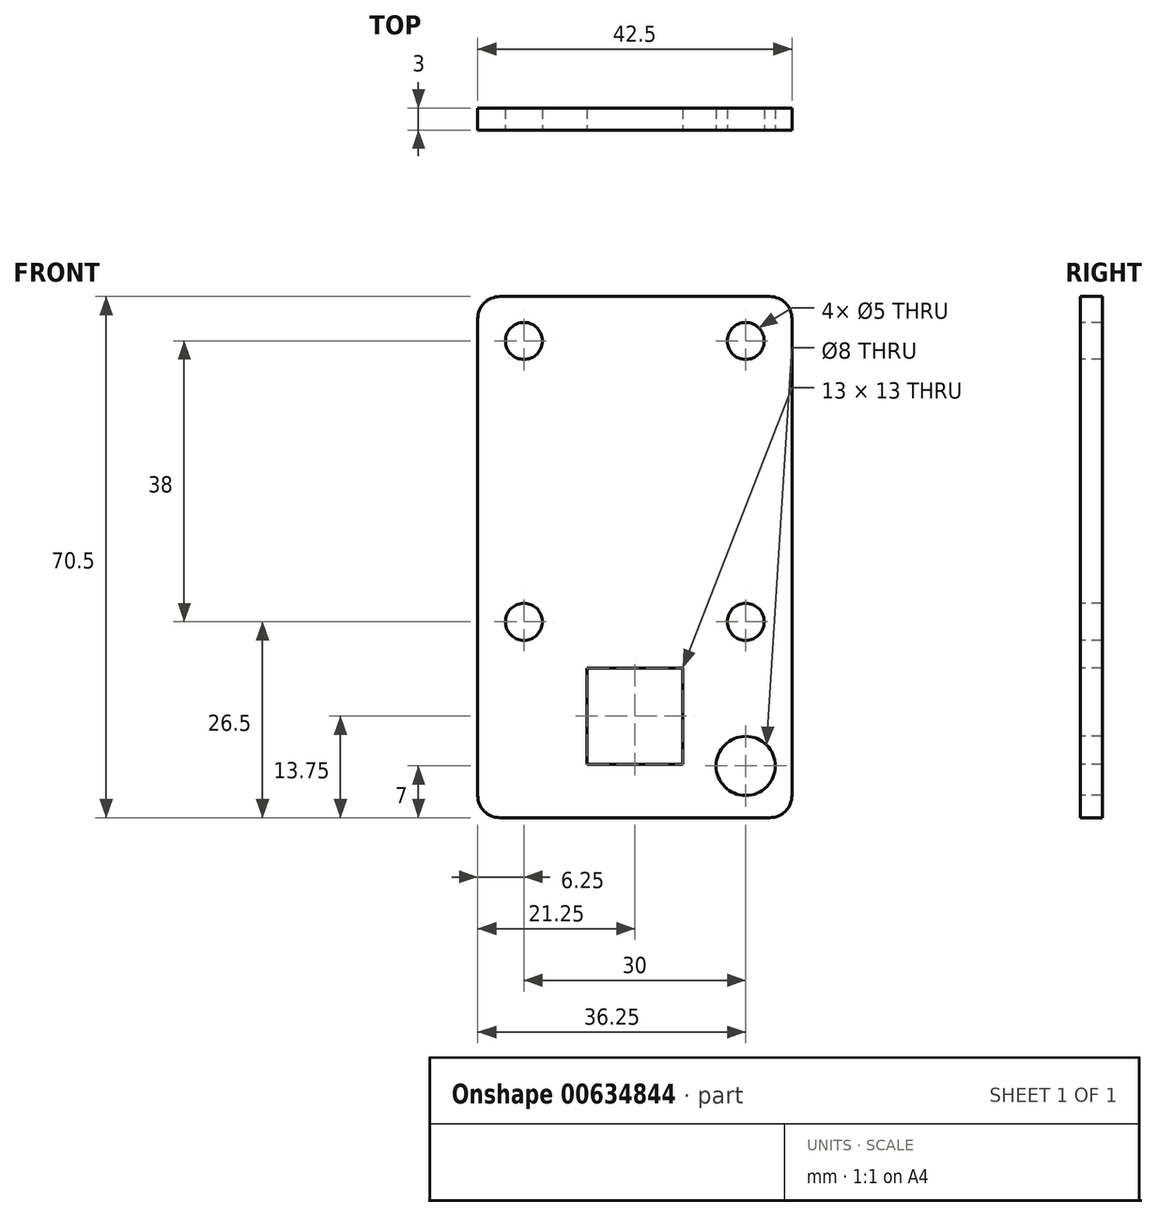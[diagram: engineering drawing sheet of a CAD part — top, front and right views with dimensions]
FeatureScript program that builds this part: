
annotation { "Feature Type Name" : "Feature", "Feature Type Description" : "" }
export const myFeature = defineFeature(function(context is Context, id is Id, definition is map)
    precondition{}
    {
        {
            var Q0;
            Q0=qCreatedBy(makeId("Front.planeOp"),FACE);
            var sketch = newSketch(context, id + "F0", { "sketchPlane" : qUnion([Q0])});
            skLineSegment(sketch, "E0.bottom", {"start": v(-36.25, 63.5) * mm, "end": v(6.25, 63.5) * mm});
            skLineSegment(sketch, "E0.top", {"start": v(-36.25, -7) * mm, "end": v(6.25, -7) * mm});
            skLineSegment(sketch, "E0.left", {"start": v(-36.25, 63.5) * mm, "end": v(-36.25, -7) * mm});
            skLineSegment(sketch, "E0.right", {"start": v(6.25, 63.5) * mm, "end": v(6.25, -7) * mm});
            skCircle(sketch, "E1", {"center": v(0, 0) * mm, "radius": 4 * mm});
            skLineSegment(sketch, "E2", {"start": v(-42.48, 38.5) * mm, "end": v(13.62, 38.5) * mm, "construction": true});
            skLineSegment(sketch, "E3", {"start": v(-15, 66.75) * mm, "end": v(-15, -10.86) * mm, "construction": true});
            skPoint(sketch, "E3.startSnap0", {"position": v(-15, 63.5) * mm});
            skPoint(sketch, "E3.endSnap0", {"position": v(-15, -7) * mm});
            skCircle(sketch, "E4", {"center": v(-30, 57.5) * mm, "radius": 2.5 * mm});
            skCircle(sketch, "E5", {"center": v(-30, 19.5) * mm, "radius": 2.5 * mm});
            skCircle(sketch, "E6.MirrorC", {"center": v(0, 57.5) * mm, "radius": 2.5 * mm});
            skCircle(sketch, "E7.MirrorC", {"center": v(0, 19.5) * mm, "radius": 2.5 * mm});
            skLineSegment(sketch, "E8.bottom", {"start": v(-21.5, 13.25) * mm, "end": v(-8.5, 13.25) * mm});
            skLineSegment(sketch, "E8.top", {"start": v(-21.5, 0.25) * mm, "end": v(-8.5, 0.25) * mm});
            skLineSegment(sketch, "E8.left", {"start": v(-21.5, 13.25) * mm, "end": v(-21.5, 0.25) * mm});
            skLineSegment(sketch, "E8.right", {"start": v(-8.5, 13.25) * mm, "end": v(-8.5, 0.25) * mm});
            skSolve(sketch);
        }
        {
            var Q0;
            Q0=makeQuery(id+"F0.imprint","IMPRINT",FACE,{"disambiguationData":[TD([[makeQuery(id+"F0.imprint","IMPRINT",EDGE,{"derivedFrom":sQuery(id+"F0.wireOp",EDGE,"E0.bottom")}),-1.0]])]});
            extrude(context, id + "F1", {"entities" : qUnion([Q0]), "oppositeDirection" : true, "depth" : 3 * mm, "offsetDistance" : 25 * mm});
        }
        {
            var Q0;
            Q0=makeQuery(id+"F1.opExtrude","SWEPT_EDGE",EDGE,{"disambiguationData":[OSD([sQuery(id+"F0.wireOp",EDGE,"E0.bottom"),sQuery(id+"F0.wireOp",EDGE,"E0.left")])]});
            var Q1;
            Q1=makeQuery(id+"F1.opExtrude","SWEPT_EDGE",EDGE,{"disambiguationData":[OSD([sQuery(id+"F0.wireOp",EDGE,"E0.bottom"),sQuery(id+"F0.wireOp",EDGE,"E0.right")])]});
            var Q2;
            Q2=makeQuery(id+"F1.opExtrude","SWEPT_EDGE",EDGE,{"disambiguationData":[OSD([sQuery(id+"F0.wireOp",EDGE,"E0.top"),sQuery(id+"F0.wireOp",EDGE,"E0.right")])]});
            var Q3;
            Q3=makeQuery(id+"F1.opExtrude","SWEPT_EDGE",EDGE,{"disambiguationData":[OSD([sQuery(id+"F0.wireOp",EDGE,"E0.top"),sQuery(id+"F0.wireOp",EDGE,"E0.left")])]});
            fillet(context, id + "F2", {"entities" : qUnion([Q0, Q1, Q2, Q3]), "radius" : 3 * mm, "tangentPropagation" : true, "allowEdgeOverflow" : false});
        }
    });
